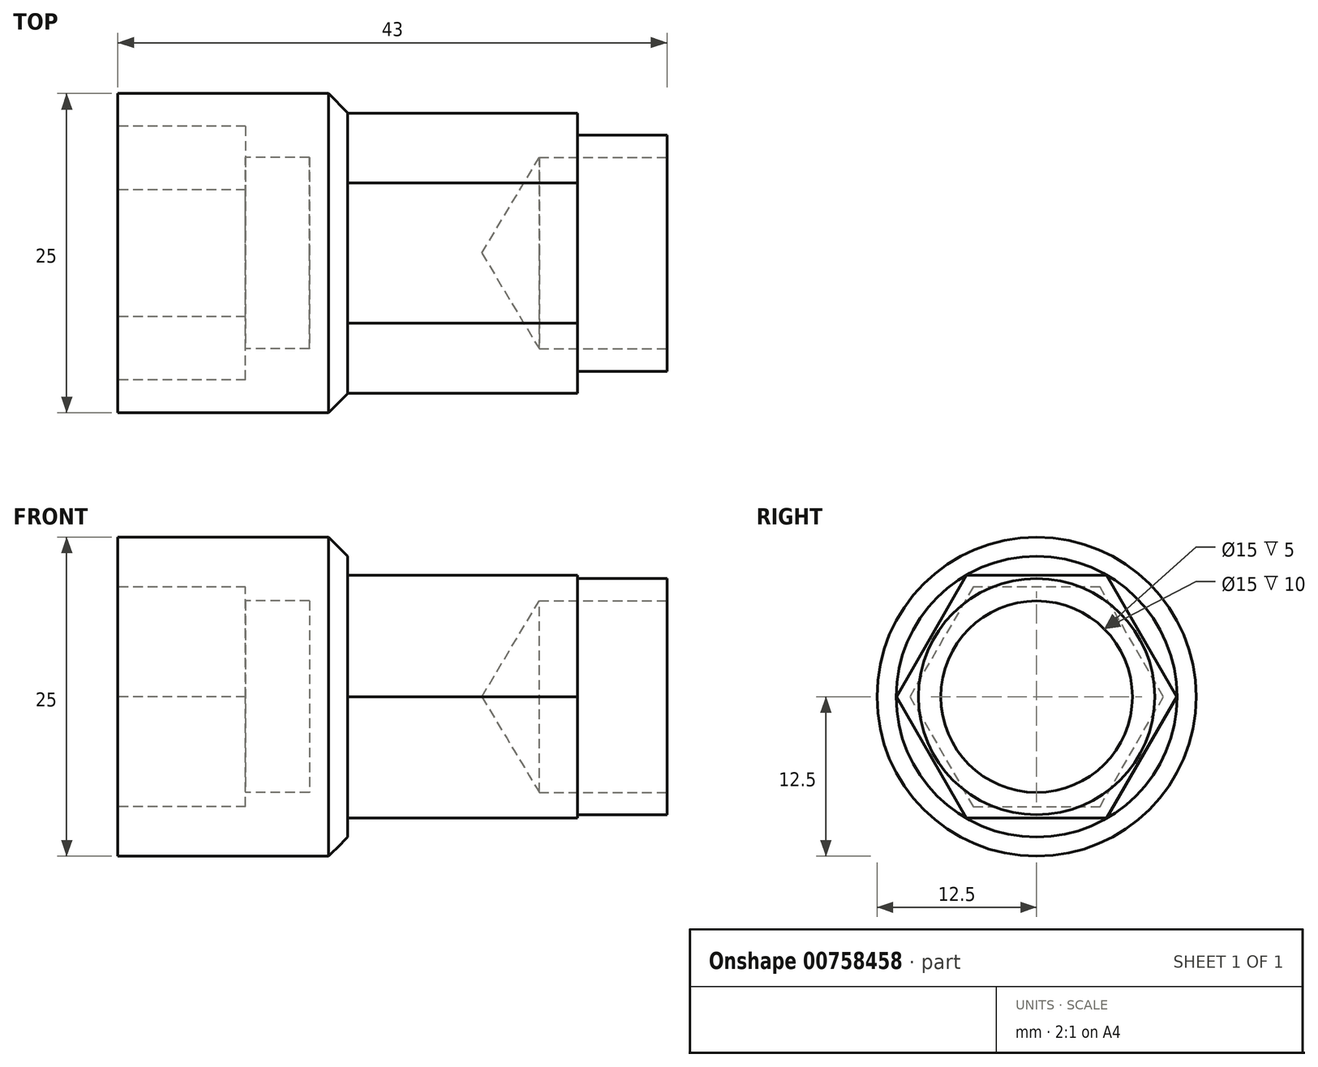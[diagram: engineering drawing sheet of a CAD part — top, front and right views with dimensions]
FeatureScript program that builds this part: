
annotation { "Feature Type Name" : "Feature", "Feature Type Description" : "" }
export const myFeature = defineFeature(function(context is Context, id is Id, definition is map)
    precondition{}
    {
        {
            var Q0;
            Q0=qCreatedBy(makeId("Top.planeOp"),FACE);
            var sketch = newSketch(context, id + "F0", { "sketchPlane" : qUnion([Q0])});
            skLineSegment(sketch, "E0", {"start": v(0, 8.5) * mm, "end": v(0, 12.5) * mm});
            skLineSegment(sketch, "E1", {"start": v(0, 12.5) * mm, "end": v(18, 12.5) * mm});
            skLineSegment(sketch, "E2", {"start": v(18, 12.5) * mm, "end": v(18, 0) * mm});
            skLineSegment(sketch, "E3", {"start": v(0, 8.5) * mm, "end": v(10, 8.5) * mm});
            skLineSegment(sketch, "E4", {"start": v(15, 0) * mm, "end": v(18, 0) * mm});
            skLineSegment(sketch, "E5", {"start": v(10, 8.5) * mm, "end": v(10, 7.5) * mm});
            skLineSegment(sketch, "E6", {"start": v(10, 7.5) * mm, "end": v(15, 7.5) * mm});
            skLineSegment(sketch, "E7", {"start": v(15, 7.5) * mm, "end": v(15, 0) * mm});
            skSolve(sketch);
        }
        {
            var Q0;
            Q0=makeQuery(id+"F0.imprint","IMPRINT",FACE,{"disambiguationData":[TD([[makeQuery(id+"F0.imprint","IMPRINT",EDGE,{"derivedFrom":sQuery(id+"F0.wireOp",EDGE,"E0")}),-1.0]])]});
            var Q1;
            Q1=sQuery(id+"F0.wireOp",EDGE,"E4");
            revolve(context, id + "F1", {"surfaceOperationType" : NewSurfaceOperationType.NEW, "entities" : qUnion([Q0]), "axis" : qUnion([Q1]), "revolveType" : RevolveType.FULL});
        }
        {
            var Q0;
            Q0=makeQuery(id+"F1.opRevolve","SWEPT_FACE",FACE,{"disambiguationData":[OSD([sQuery(id+"F0.wireOp",EDGE,"E0")])]});
            var sketch = newSketch(context, id + "F2", { "sketchPlane" : qUnion([Q0])});
            skCircle(sketch, "E8.cCircle", {"center": v(0, 0) * mm, "radius": 8.6 * mm});
            skLineSegment(sketch, "E8.0", {"start": v(-4.97, 8.6) * mm, "end": v(4.97, 8.6) * mm});
            skLineSegment(sketch, "E8.1", {"start": v(4.97, 8.6) * mm, "end": v(9.93, 0) * mm});
            skLineSegment(sketch, "E8.2", {"start": v(9.93, 0) * mm, "end": v(4.97, -8.6) * mm});
            skLineSegment(sketch, "E8.3", {"start": v(4.97, -8.6) * mm, "end": v(-4.97, -8.6) * mm});
            skLineSegment(sketch, "E8.4", {"start": v(-4.97, -8.6) * mm, "end": v(-9.93, 0) * mm});
            skLineSegment(sketch, "E8.5", {"start": v(-9.93, 0) * mm, "end": v(-4.97, 8.6) * mm});
            skPoint(sketch, "E8.0.midPoint", {"position": v(0, 8.6) * mm});
            skSolve(sketch);
        }
        {
            var Q0;
            Q0 = qSketchRegion(id + "F2", true);
            extrude(context, id + "F3", {"entities" : qUnion([Q0]), "operationType" : NewBodyOperationType.REMOVE, "oppositeDirection" : true, "depth" : 10 * mm, "offsetDistance" : 25 * mm});
        }
        {
            var Q0;
            Q0=makeQuery(id+"F1.opRevolve","SWEPT_FACE",FACE,{"disambiguationData":[OSD([sQuery(id+"F0.wireOp",EDGE,"E2")])]});
            var sketch = newSketch(context, id + "F4", { "sketchPlane" : qUnion([Q0])});
            skCircle(sketch, "E9.cCircle", {"center": v(0, 0) * mm, "radius": 9.5 * mm, "construction": true});
            skLineSegment(sketch, "E9.0", {"start": v(-5.48, 9.5) * mm, "end": v(5.48, 9.5) * mm});
            skLineSegment(sketch, "E9.1", {"start": v(5.48, 9.5) * mm, "end": v(10.97, 0) * mm});
            skLineSegment(sketch, "E9.2", {"start": v(10.97, 0) * mm, "end": v(5.48, -9.5) * mm});
            skLineSegment(sketch, "E9.3", {"start": v(5.48, -9.5) * mm, "end": v(-5.48, -9.5) * mm});
            skLineSegment(sketch, "E9.4", {"start": v(-5.48, -9.5) * mm, "end": v(-10.97, 0) * mm});
            skLineSegment(sketch, "E9.5", {"start": v(-10.97, 0) * mm, "end": v(-5.48, 9.5) * mm});
            skPoint(sketch, "E9.0.midPoint", {"position": v(0, 9.5) * mm});
            skSolve(sketch);
        }
        {
            var Q0;
            Q0 = qSketchRegion(id + "F4", true);
            extrude(context, id + "F5", {"entities" : qUnion([Q0]), "operationType" : NewBodyOperationType.ADD, "depth" : 18 * mm, "offsetDistance" : 25 * mm});
        }
        {
            var Q0;
            Q0=makeQuery(id+"F5.opExtrude","CAP_FACE",FACE,{"disambiguationData":[OSD([sQuery(id+"F4.wireOp",EDGE,"E9.0"),sQuery(id+"F4.wireOp",EDGE,"E9.1"),sQuery(id+"F4.wireOp",EDGE,"E9.2"),sQuery(id+"F4.wireOp",EDGE,"E9.3"),sQuery(id+"F4.wireOp",EDGE,"E9.4"),sQuery(id+"F4.wireOp",EDGE,"E9.5")])],"isStart":false});
            var sketch = newSketch(context, id + "F6", { "sketchPlane" : qUnion([Q0])});
            skCircle(sketch, "E10", {"center": v(0, 0) * mm, "radius": 9.25 * mm});
            skSolve(sketch);
        }
        {
            var Q0;
            Q0 = qSketchRegion(id + "F6", true);
            extrude(context, id + "F7", {"entities" : qUnion([Q0]), "operationType" : NewBodyOperationType.ADD, "depth" : 7 * mm, "offsetDistance" : 25 * mm});
        }
        {
            var Q0;
            Q0=makeQuery(id+"F1.opRevolve","SWEPT_EDGE",EDGE,{"disambiguationData":[OSD([sQuery(id+"F0.wireOp",EDGE,"E1"),sQuery(id+"F0.wireOp",EDGE,"E2")])]});
            chamfer(context, id + "F8", {"entities" : qUnion([Q0]), "width" : 1.5 * mm, "tangentPropagation" : true});
        }
        {
            var Q0;
            Q0=makeQuery(id+"F7.opExtrude","CAP_FACE",FACE,{"disambiguationData":[OSD([sQuery(id+"F6.wireOp",EDGE,"E10")])],"isStart":false});
            var sketch = newSketch(context, id + "F9", { "sketchPlane" : qUnion([Q0])});
            skPoint(sketch, "E11", {"position": v(0, 0) * mm});
            skSolve(sketch);
        }
        {
            var Q0;
            Q0=sQuery(id+"F9.wireOp",VERTEX,"E11");
            var Q1;
            Q1=makeQuery(id+"F1.opRevolve","SWEPT_BODY",BODY,{"disambiguationData":[OSD([sQuery(id+"F0.wireOp",EDGE,"E0"),sQuery(id+"F0.wireOp",EDGE,"E1"),sQuery(id+"F0.wireOp",EDGE,"E2"),sQuery(id+"F0.wireOp",EDGE,"E3"),sQuery(id+"F0.wireOp",EDGE,"E4"),sQuery(id+"F0.wireOp",EDGE,"E5"),sQuery(id+"F0.wireOp",EDGE,"E6"),sQuery(id+"F0.wireOp",EDGE,"E7")])]});
            hole(context, id + "F10", {"style" : HoleStyle.SIMPLE, "endStyle" : HoleEndStyle.BLIND, "holeDiameter" : 15 * mm, "majorDiameter" : 8 * mm, "holeDepth" : 10 * mm, "tappedDepth" : 22.5 * mm, "tapClearance" : 2, "locations" : qUnion([Q0]), "scope" : qUnion([Q1])});
        }
    });
